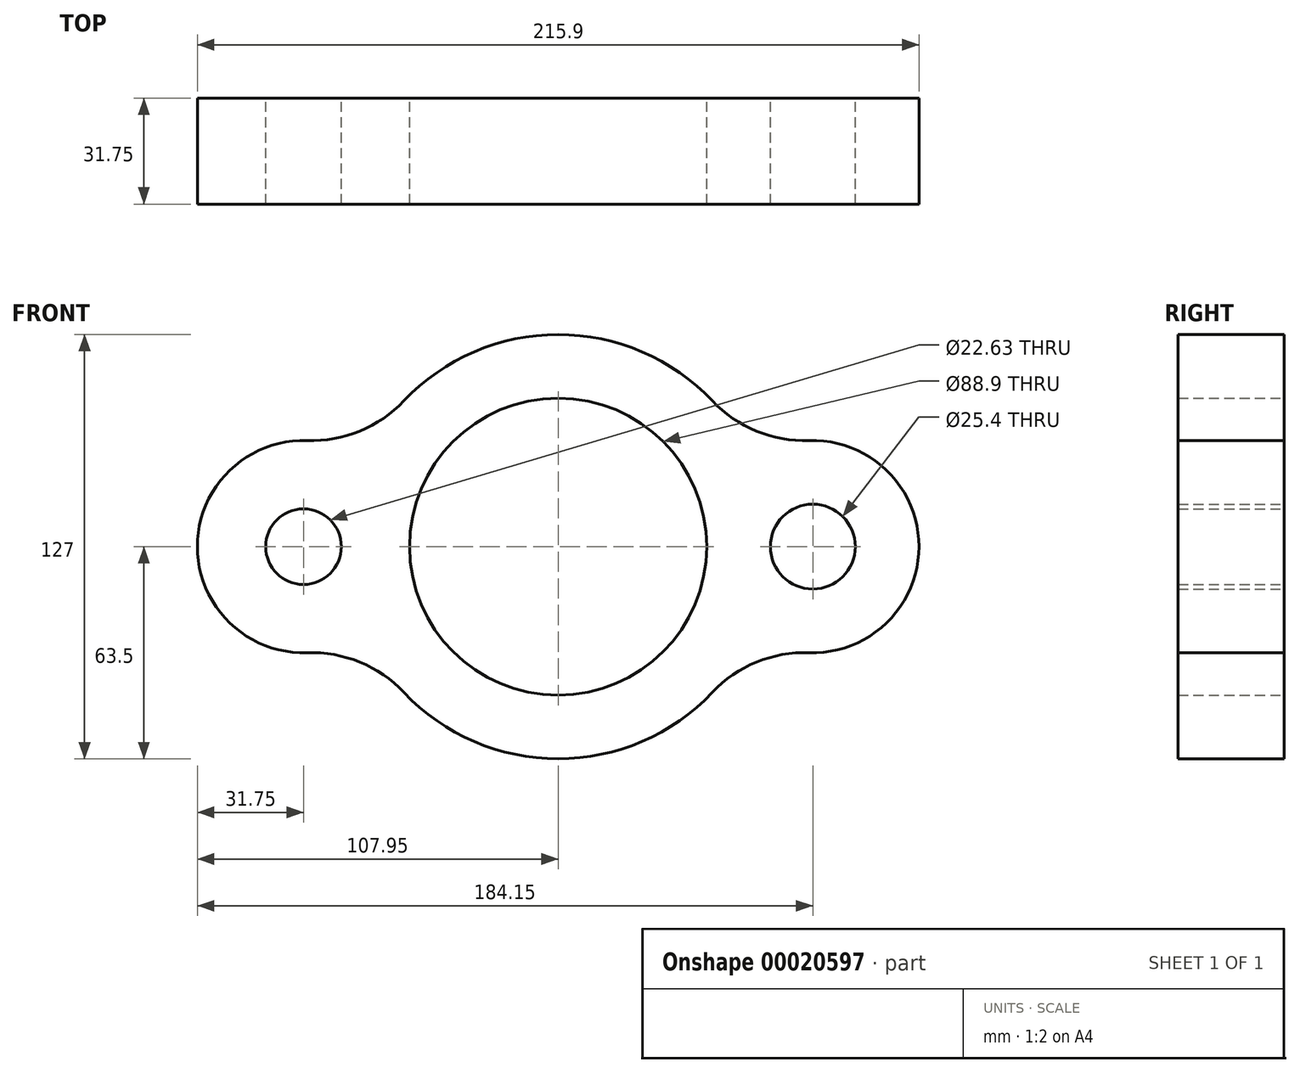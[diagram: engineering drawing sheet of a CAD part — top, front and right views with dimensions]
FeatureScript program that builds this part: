
annotation { "Feature Type Name" : "Feature", "Feature Type Description" : "" }
export const myFeature = defineFeature(function(context is Context, id is Id, definition is map)
    precondition{}
    {
        {
            var Q0;
            Q0=qCreatedBy(makeId("Front.planeOp"),FACE);
            var sketch = newSketch(context, id + "F0", { "sketchPlane" : qUnion([Q0])});
            skCircle(sketch, "E0", {"center": v(0, 0) * mm, "radius": 44.45 * mm});
            skArc(sketch, "E1", {"start": v(-46.14, -43.63) * mm, "mid": v(0, -63.5) * mm, "end": v(46.14, -43.63) * mm});
            skPoint(sketch, "E2.center.orphan", {"position": v(-81.26, 0) * mm});
            skCircle(sketch, "E3", {"center": v(-76.2, 0) * mm, "radius": 11.32 * mm});
            skArc(sketch, "E4", {"start": v(-75.12, 31.73) * mm, "mid": v(-107.95, 0) * mm, "end": v(-75.12, -31.73) * mm});
            skPoint(sketch, "E5.center.orphan", {"position": v(77.91, 0) * mm});
            skCircle(sketch, "E6", {"center": v(76.2, 0) * mm, "radius": 12.7 * mm});
            skArc(sketch, "E7", {"start": v(75.12, -31.73) * mm, "mid": v(107.95, 0) * mm, "end": v(75.12, 31.73) * mm});
            skArc(sketch, "E8.trimOffspring", {"start": v(46.14, 43.63) * mm, "mid": v(0, 63.5) * mm, "end": v(-46.14, 43.63) * mm});
            skPoint(sketch, "E9.visualSharp", {"position": v(57.94, 25.98) * mm});
            skArc(sketch, "E9.filletArc", {"start": v(46.14, 43.63) * mm, "mid": v(59.35, 34.56) * mm, "end": v(75.12, 31.73) * mm});
            skPoint(sketch, "E10.visualSharp", {"position": v(-57.94, 25.98) * mm});
            skArc(sketch, "E10.filletArc", {"start": v(-75.12, 31.73) * mm, "mid": v(-59.35, 34.56) * mm, "end": v(-46.14, 43.63) * mm});
            skPoint(sketch, "E11.visualSharp", {"position": v(-57.94, -25.98) * mm});
            skArc(sketch, "E11.filletArc", {"start": v(-46.14, -43.63) * mm, "mid": v(-59.35, -34.56) * mm, "end": v(-75.12, -31.73) * mm});
            skPoint(sketch, "E12.visualSharp", {"position": v(57.94, -25.98) * mm});
            skArc(sketch, "E12.filletArc", {"start": v(75.12, -31.73) * mm, "mid": v(59.35, -34.56) * mm, "end": v(46.14, -43.63) * mm});
            skSolve(sketch);
        }
        {
            var Q0;
            Q0=makeQuery(id+"F0.imprint","IMPRINT",FACE,{"disambiguationData":[TD([[makeQuery(id+"F0.imprint","IMPRINT",EDGE,{"derivedFrom":sQuery(id+"F0.wireOp",EDGE,"E1")}),1.0]])]});
            extrude(context, id + "F1", {"entities" : qUnion([Q0]), "depth" : 6.35 * mm});
        }
        {
            var Q0;
            Q0=makeQuery(id+"F1.opExtrude","CAP_FACE",FACE,{"disambiguationData":[OSD([sQuery(id+"F0.wireOp",EDGE,"E0"),sQuery(id+"F0.wireOp",EDGE,"E1"),sQuery(id+"F0.wireOp",EDGE,"E3"),sQuery(id+"F0.wireOp",EDGE,"E4"),sQuery(id+"F0.wireOp",EDGE,"E6"),sQuery(id+"F0.wireOp",EDGE,"E7"),sQuery(id+"F0.wireOp",EDGE,"E8.trimOffspring"),sQuery(id+"F0.wireOp",EDGE,"E9.filletArc"),sQuery(id+"F0.wireOp",EDGE,"E10.filletArc"),sQuery(id+"F0.wireOp",EDGE,"E11.filletArc"),sQuery(id+"F0.wireOp",EDGE,"E12.filletArc")])],"isStart":false});
            extrude(context, id + "F2", {"entities" : qUnion([Q0]), "operationType" : NewBodyOperationType.ADD, "depth" : 25.4 * mm});
        }
    });
